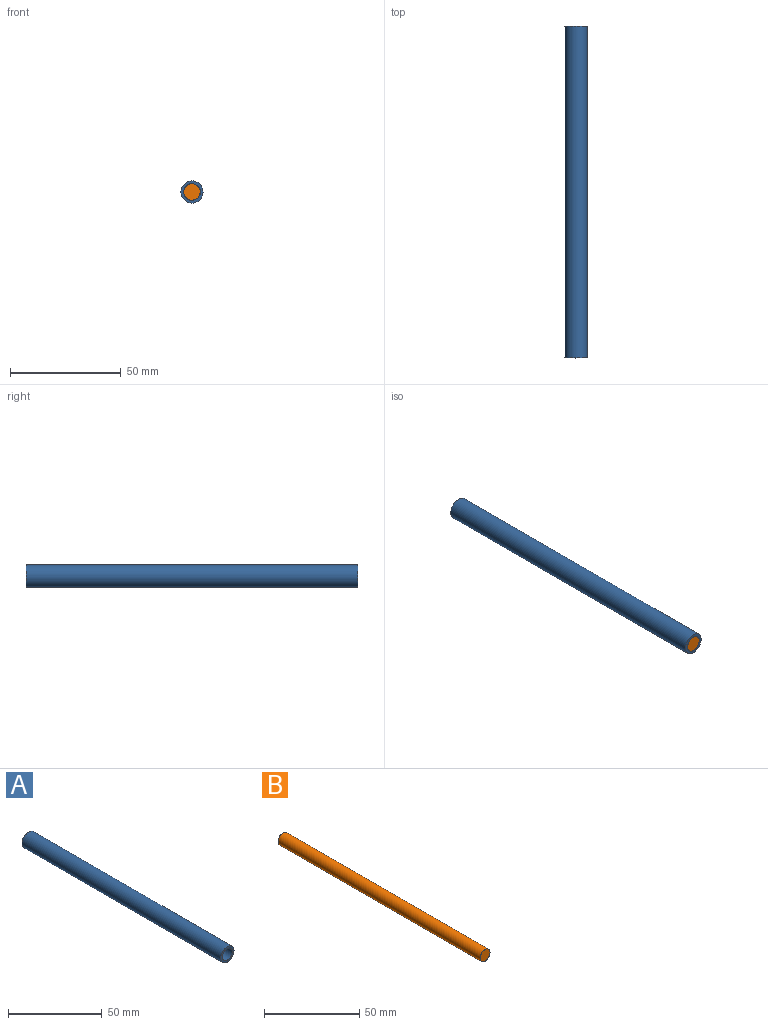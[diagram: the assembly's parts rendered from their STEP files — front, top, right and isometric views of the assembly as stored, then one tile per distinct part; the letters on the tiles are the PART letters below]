
ASSEMBLY  parts=2 mates=1
PART A: 4 faces, bbox 10x150x10 mm
  f0: cylinder r=5mm len=150mm, axis (0,1,0), area 4712.4mm2, adj f1,f2
  f1: plane 10x10mm, normal (0,-1,0), area 33.9mm2, adj f0,f3
  f2: plane 10x10mm, normal (0,1,0), area 33.9mm2, adj f0,f3
  f3: cylinder r=3.77mm len=150mm, axis (0,-1,0), area 3554.5mm2, adj f1,f2
PART B: 3 faces, bbox 7.4x150x7.4 mm
  f0: cylinder r=3.7mm len=150mm, axis (0,1,0), area 3487.2mm2, adj f1,f2
  f1: plane 7.4x7.4mm, normal (0,-1,0), area 43mm2, adj f0
  f2: plane 7.4x7.4mm, normal (0,1,0), area 43mm2, adj f0
PLACE A t=(-30.2,65.97,-6.3)mm
PLACE B t=(-30.2,65.97,-6.3)mm
MATE fastened B.f0 <-> A.f0  axis (0,-1,0) through (-30.2,-84.03,-6.3)mm
